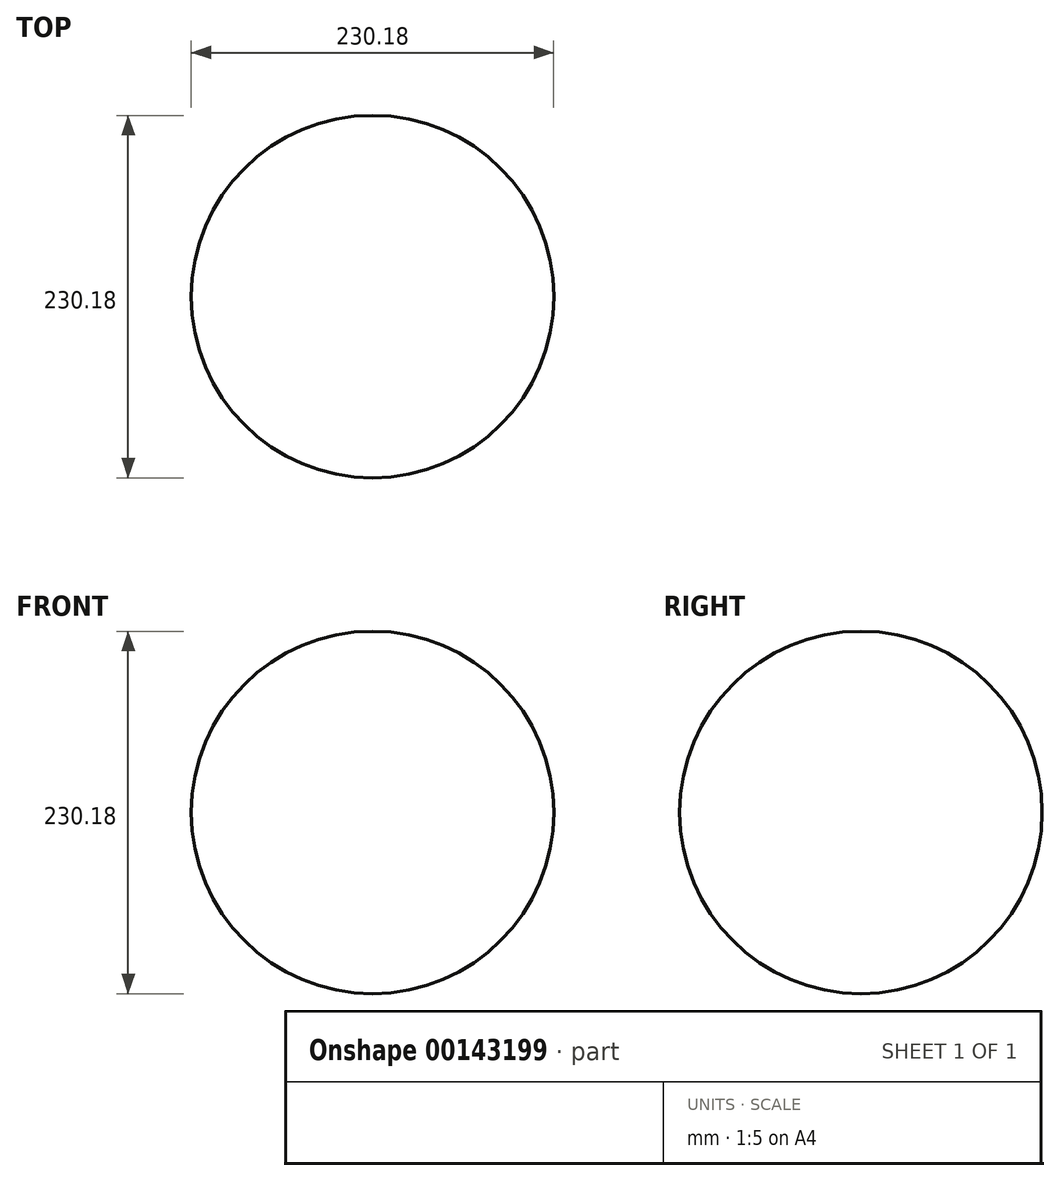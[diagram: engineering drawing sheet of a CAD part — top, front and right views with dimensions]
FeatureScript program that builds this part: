
annotation { "Feature Type Name" : "Feature", "Feature Type Description" : "" }
export const myFeature = defineFeature(function(context is Context, id is Id, definition is map)
    precondition{}
    {
        {
            var Q0;
            Q0=qCreatedBy(makeId("Top.planeOp"),FACE);
            var sketch = newSketch(context, id + "F0", { "sketchPlane" : qUnion([Q0])});
            skCircle(sketch, "E0", {"center": v(-195.28, 162.35) * mm, "radius": 115.1 * mm});
            skArc(sketch, "E1", {"start": v(-273.52, -131.85) * mm, "mid": v(-179.9, -180) * mm, "end": v(-86.28, -131.85) * mm});
            skLineSegment(sketch, "E2", {"start": v(-83.7, -130.52) * mm, "end": v(-37.19, -130.52) * mm});
            skLineSegment(sketch, "E3", {"start": v(-276.1, -130.52) * mm, "end": v(-317.44, -130.52) * mm});
            skLineSegment(sketch, "E4", {"start": v(-323.74, -136.11) * mm, "end": v(-323.74, -232.12) * mm});
            skLineSegment(sketch, "E5", {"start": v(-30.9, -136.02) * mm, "end": v(-30.9, -232.12) * mm});
            skLineSegment(sketch, "E6", {"start": v(323.74, -135) * mm, "end": v(323.74, -232.12) * mm});
            skLineSegment(sketch, "E7", {"start": v(80.18, -130.52) * mm, "end": v(37.22, -130.52) * mm});
            skLineSegment(sketch, "E8", {"start": v(274.46, -130.52) * mm, "end": v(317.67, -130.52) * mm});
            skArc(sketch, "E9", {"start": v(82.8, -131.88) * mm, "mid": v(119.86, -165.95) * mm, "end": v(167.93, -180.94) * mm});
            skLineSegment(sketch, "E10", {"start": v(30.9, -232.12) * mm, "end": v(323.74, -232.12) * mm});
            skLineSegment(sketch, "E11", {"start": v(-30.9, -232.12) * mm, "end": v(-167.67, -232.12) * mm});
            skArc(sketch, "E12", {"start": v(-167.67, -232.12) * mm, "mid": v(-169.91, -231.2) * mm, "end": v(-170.84, -228.95) * mm});
            skLineSegment(sketch, "E13", {"start": v(-170.84, -228.95) * mm, "end": v(-170.84, -206.73) * mm});
            skLineSegment(sketch, "E14", {"start": v(-183.8, -206.73) * mm, "end": v(-183.8, -228.95) * mm});
            skArc(sketch, "E15", {"start": v(-183.8, -228.95) * mm, "mid": v(-184.73, -231.2) * mm, "end": v(-186.97, -232.12) * mm});
            skLineSegment(sketch, "E16", {"start": v(-186.97, -232.12) * mm, "end": v(-323.74, -232.12) * mm});
            skLineSegment(sketch, "E17", {"start": v(183.8, -206.72) * mm, "end": v(183.8, -184.1) * mm});
            skLineSegment(sketch, "E18", {"start": v(170.84, -184) * mm, "end": v(170.84, -206.72) * mm});
            skArc(sketch, "E19", {"start": v(186.71, -180.94) * mm, "mid": v(234.78, -165.95) * mm, "end": v(271.85, -131.88) * mm});
            skArc(sketch, "E20", {"start": v(170.84, -184.1) * mm, "mid": v(170, -181.95) * mm, "end": v(167.93, -180.94) * mm});
            skArc(sketch, "E21", {"start": v(186.71, -180.94) * mm, "mid": v(184.64, -181.95) * mm, "end": v(183.8, -184.1) * mm});
            skArc(sketch, "E22", {"start": v(-30.84, -136.87) * mm, "mid": v(-32.7, -132.38) * mm, "end": v(-37.19, -130.52) * mm});
            skArc(sketch, "E23", {"start": v(-317.44, -130.52) * mm, "mid": v(-321.93, -132.38) * mm, "end": v(-323.79, -136.87) * mm});
            skArc(sketch, "E24", {"start": v(37.22, -130.52) * mm, "mid": v(32.73, -132.38) * mm, "end": v(30.87, -136.87) * mm});
            skArc(sketch, "E25", {"start": v(324.02, -136.87) * mm, "mid": v(322.16, -132.38) * mm, "end": v(317.67, -130.52) * mm});
            skLineSegment(sketch, "E26", {"start": v(-195.28, 277.44) * mm, "end": v(-195.28, 47.26) * mm});
            skLineSegment(sketch, "E27.top", {"start": v(183.8, -206.72) * mm, "end": v(170.84, -206.72) * mm});
            skLineSegment(sketch, "E28.top", {"start": v(-170.84, -206.73) * mm, "end": v(-183.8, -206.73) * mm});
            skPoint(sketch, "E29.visualSharp", {"position": v(-274.46, -130.52) * mm});
            skArc(sketch, "E29.filletArc", {"start": v(-273.52, -131.85) * mm, "mid": v(-274.65, -130.87) * mm, "end": v(-276.1, -130.52) * mm});
            skPoint(sketch, "E30.visualSharp", {"position": v(-85.35, -130.52) * mm});
            skArc(sketch, "E30.filletArc", {"start": v(-83.7, -130.52) * mm, "mid": v(-85.15, -130.87) * mm, "end": v(-86.28, -131.85) * mm});
            skPoint(sketch, "E31.visualSharp", {"position": v(81.86, -130.52) * mm});
            skArc(sketch, "E31.filletArc", {"start": v(82.8, -131.88) * mm, "mid": v(81.65, -130.88) * mm, "end": v(80.18, -130.52) * mm});
            skPoint(sketch, "E32.visualSharp", {"position": v(272.78, -130.52) * mm});
            skArc(sketch, "E32.filletArc", {"start": v(274.46, -130.52) * mm, "mid": v(272.98, -130.88) * mm, "end": v(271.85, -131.88) * mm});
            skLineSegment(sketch, "E33", {"start": v(30.87, -136.87) * mm, "end": v(30.9, -232.12) * mm});
            skSolve(sketch);
        }
        {
            var Q0;
            {var subQ0=sQuery(id+"F0.wireOp",EDGE,"E26");Q0=makeQuery(id+"F0.imprint","IMPRINT",FACE,{"disambiguationData":[TD([[makeQuery(id+"F0.imprint","IMPRINT",EDGE,{"derivedFrom":subQ0}),-1.0]])]});}
            var Q1;
            Q1=sQuery(id+"F0.wireOp",EDGE,"E26");
            revolve(context, id + "F1", {"entities" : qUnion([Q0]), "axis" : qUnion([Q1]), "revolveType" : RevolveType.FULL});
        }
    });
